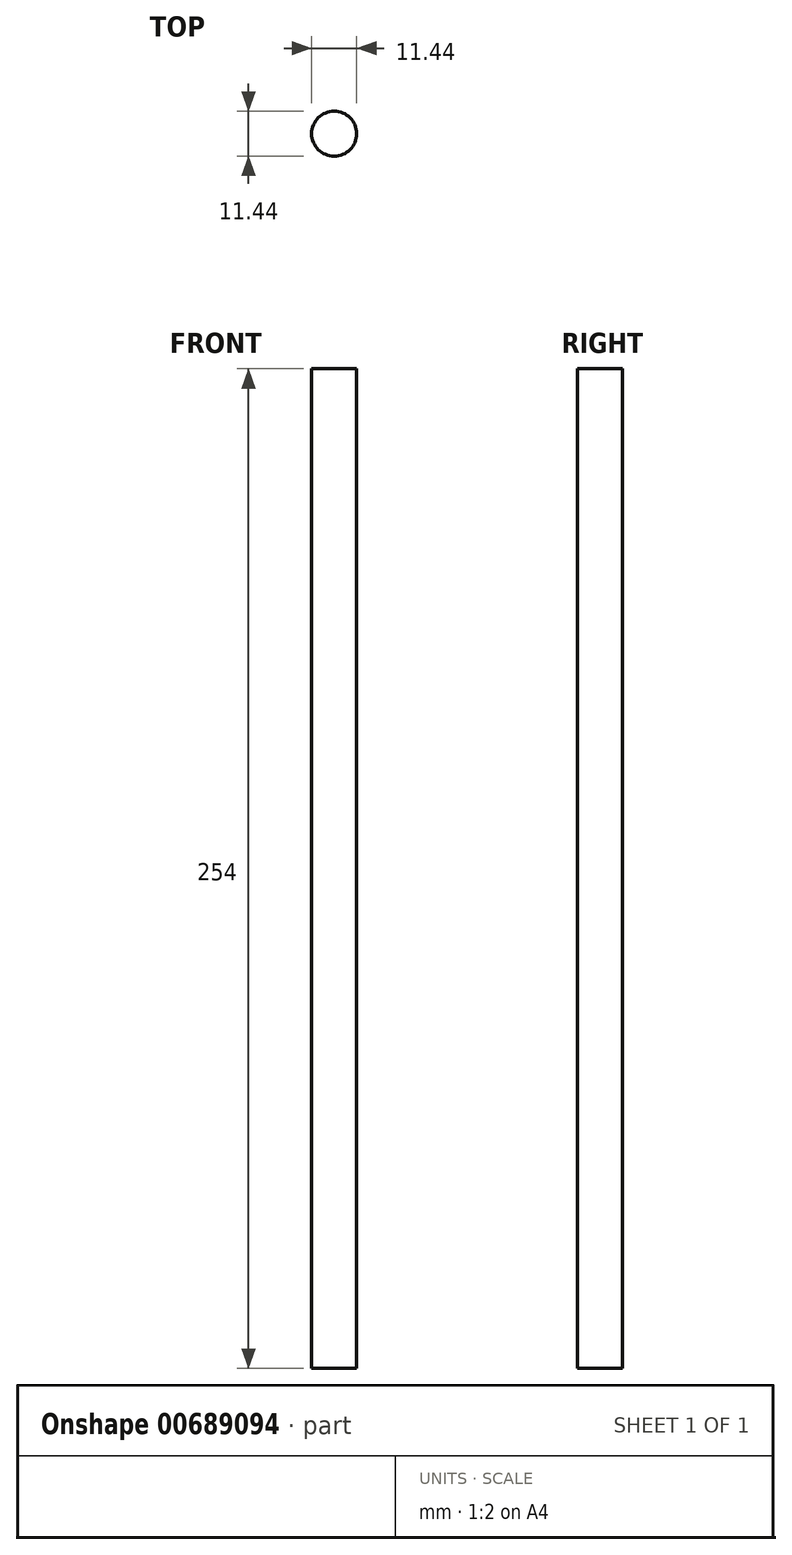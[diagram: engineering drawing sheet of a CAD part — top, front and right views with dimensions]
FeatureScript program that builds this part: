
annotation { "Feature Type Name" : "Feature", "Feature Type Description" : "" }
export const myFeature = defineFeature(function(context is Context, id is Id, definition is map)
    precondition{}
    {
        {
            var Q0;
            Q0=qCreatedBy(makeId("Top.planeOp"),FACE);
            var sketch = newSketch(context, id + "F0", { "sketchPlane" : qUnion([Q0])});
            skCircle(sketch, "E0", {"center": v(0, 0) * mm, "radius": 5.72 * mm});
            skSolve(sketch);
        }
        {
            var Q0;
            Q0 = qSketchRegion(id + "F0", true);
            extrude(context, id + "F1", {"entities" : qUnion([Q0]), "depth" : 127 * mm, "offsetDistance" : 25.4 * mm, "hasSecondDirection" : true, "secondDirectionOppositeDirection" : true, "secondDirectionDepth" : 127 * mm});
        }
    });
